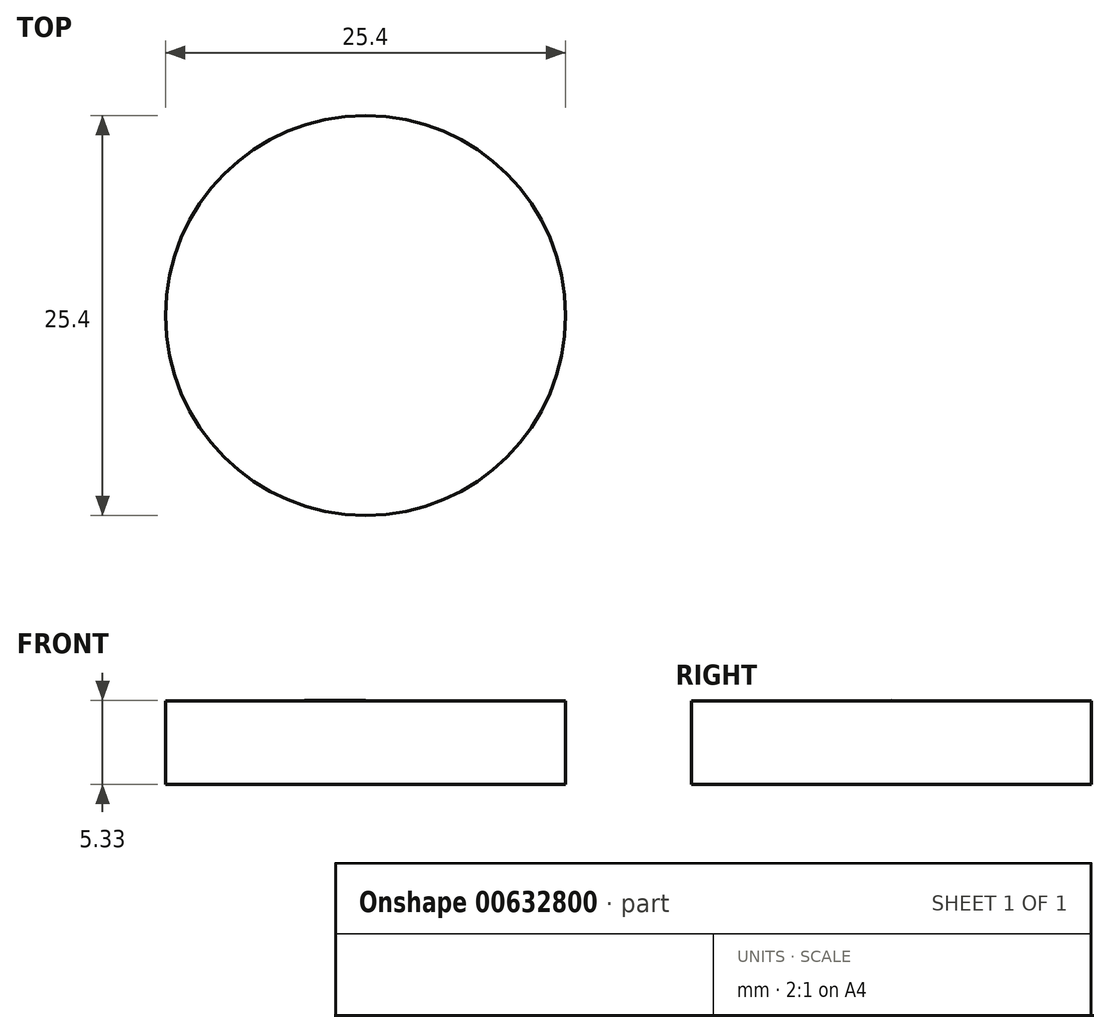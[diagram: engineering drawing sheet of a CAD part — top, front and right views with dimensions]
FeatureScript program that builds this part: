
annotation { "Feature Type Name" : "Feature", "Feature Type Description" : "" }
export const myFeature = defineFeature(function(context is Context, id is Id, definition is map)
    precondition{}
    {
        {
            var Q0;
            Q0=qCreatedBy(makeId("Front.planeOp"),FACE);
            var sketch = newSketch(context, id + "F0", { "sketchPlane" : qUnion([Q0])});
            skLineSegment(sketch, "E0.bottom", {"start": v(0, 0) * mm, "end": v(-12.7, 0) * mm});
            skLineSegment(sketch, "E0.left", {"start": v(0, 0) * mm, "end": v(0, 8.38) * mm});
            skPoint(sketch, "E1", {"position": v(-12.7, 8.38) * mm});
            skPoint(sketch, "E2", {"position": v(-12.7, 0) * mm});
            skLineSegment(sketch, "E3", {"start": v(-12.7, 0) * mm, "end": v(-12.7, 8.38) * mm});
            skLineSegment(sketch, "E4", {"start": v(-12.7, 8.38) * mm, "end": v(0, 8.38) * mm});
            skLineSegment(sketch, "E5", {"start": v(0, 8.38) * mm, "end": v(0, 8.38) * mm});
            skLineSegment(sketch, "E6", {"start": v(-12.7, 5.33) * mm, "end": v(0, 5.29) * mm});
            skSolve(sketch);
        }
        {
            var Q0;
            Q0=makeQuery(id+"F0.imprint","IMPRINT",FACE,{"disambiguationData":[TD([[makeQuery(id+"F0.imprint","IMPRINT",EDGE,{"derivedFrom":sQuery(id+"F0.wireOp",EDGE,"E0.bottom")}),-1.0]])]});
            var Q1;
            Q1=sQuery(id+"F0.wireOp",EDGE,"E3");
            revolve(context, id + "F1", {"entities" : qUnion([Q0]), "axis" : qUnion([Q1]), "revolveType" : RevolveType.FULL});
        }
    });
